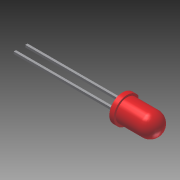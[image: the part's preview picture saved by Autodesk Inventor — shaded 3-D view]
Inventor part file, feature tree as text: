
AUTODESK INVENTOR PART (.ipt)
format: ipt  version: 2015 (Build 190159000, 159)  size: 212,992 bytes
history: native  units: mm
features: other x99, extrude x2, revolve x1, sketch x1, projected_geometry x1
ambient origin geometry x8: Origin, YZ Plane, XZ Plane, XY Plane, X Axis, Y Axis, Z Axis, Center Point
bodies: Solid1 (feature_tree)
feature tree (104):
  other  "Table"
  other  "LED Heigth mm 1.0"
  other  "LED Heigth mm 1.2"
  other  "LED Heigth mm 1.4"
  other  "LED Heigth mm 1.6"
  other  "LED Heigth mm 1.8"
  other  "LED Heigth mm 2.0"
  other  "LED Heigth mm 2.2"
  other  "LED Heigth mm 2.4"
  other  "LED Heigth mm 2.6"
  other  "LED  Heigth mm 2.8"
  other  "LED Heigth mm 3.0"
  other  "LED Heigth mm 3.2"
  other  "LED Heigth mm 3.4"
  other  "LED Heigth mm 3.6"
  other  "LED Heigth mm 3.8"
  other  "LED Heigth mm 4.0"
  other  "LED Heigth mm 4.2"
  other  "LED Heigth mm 4.4"
  other  "LED Heigth mm 4.6"
  other  "LED Heigth mm 4.8"
  other  "LED Heigth mm 5.0"
  other  "LED Heigth mm 5.2"
  other  "LED Heigth mm 5.4"
  other  "LED Heigth mm 5.6"
  other  "LED Heigth mm 5.8"
  other  "LED Heigth mm 6.0"
  other  "LED Heigth mm 6.2"
  other  "LED Heigth mm 6.4"
  other  "LED Heigth mm 6.6"
  other  "LED Heigth mm 6.8"
  other  "LED Heigth mm 7.0"
  other  "LED Heigth mm 7.2"
  other  "LED Heigth mm 7.4"
  other  "LED Heigth mm 7.6"
  other  "LED Heigth mm 7.8"
  other  "LED Heigth mm 8.0"
  other  "LED Heigth mm 8.2"
  other  "LED Heigth mm 8.4"
  other  "LED Heigth mm 8.6"
  other  "LED Heigth mm 8.8"
  other  "LED Heigth mm 9.0"
  other  "LED Heigth mm 9.2"
  other  "LED Heigth mm 9.4"
  other  "LED Heigth mm 9.6"
  other  "LED Heigth mm 9.8"
  other  "LED Heigth mm 10.0"
  other  "LED Heigth mm 10.2"
  other  "LED Heigth mm 10.4"
  other  "LED Heigth mm 10.6"
  other  "LED Heigth mm 10.8"
  other  "LED Heigth mm 11.0"
  other  "LED Heigth mm 11.2"
  other  "LED Heigth mm 11.4"
  other  "LED Heigth mm 11.6"
  other  "LED Heigth mm 11.8"
  other  "LED Heigth mm 12.0"
  other  "LED Heigth mm 12.2"
  other  "LED Heigth mm 12.4"
  other  "LED Heigth mm 12.6"
  other  "LED Heigth mm 12.8"
  other  "LED Heigth mm 13.0"
  other  "LED Heigth mm 13.2"
  other  "LED Heigth mm 13.4"
  other  "LED Heigth mm 13.6"
  other  "LED Heigth mm 13.8"
  other  "LED Heigth mm 14.0"
  other  "LED Heigth mm 14.2"
  other  "LED Heigth mm 14.4"
  other  "LED Heigth mm 14.6"
  other  "LED Heigth mm 14.8"
  other  "LED Heigth mm 15.0"
  other  "LED Heigth mm 15.2"
  other  "LED Heigth mm 15.4"
  other  "LED Heigth mm 15.6"
  other  "LED Heigth mm 15.8"
  other  "LED Heigth mm 16.0"
  other  "LED Heigth mm 16.2"
  other  "LED Heigth mm 16.4"
  other  "LED Heigth mm 16.6"
  other  "LED Heigth mm 16.8"
  other  "LED Heigth mm 17.0"
  other  "LED Heigth mm 17.2"
  other  "LED Heigth mm 17.4"
  other  "LED Heigth mm 17.6"
  other  "LED Heigth mm 17.8"
  other  "LED Heigth mm 18.0"
  other  "LED Heigth mm 18.2"
  other  "LED Heigth mm 18.4"
  other  "LED Heigth mm 18.6"
  other  "LED Heigth mm 18.8"
  other  "LED Heigth mm 19.0"
  other  "LED Heigth mm 19.2"
  other  "LED Heigth mm 19.4"
  other  "LED Heigth mm 19.6"
  other  "LED Heigth mm 19.8"
  other  "LED Heigth mm 20.0"
  revolve  "Revolution1"  [1 undecoded]
  extrude  "Extrusion1"  Depth=10.0mm
  extrude  "Extrusion2"  Depth=10.0mm
  other  "Work Axis1"
  other  "Work Axis2"
  sketch  "Sketch1"  dims[d1=2.95mm d2=1.0mm d3=5.0mm d4=8.6mm d5=2.5mm d6=90.0deg d7=0.5mm d8=0.5mm d9=1.27mm d10=1.27mm d12=0.0mm d13=20.0mm d14=0.0mm d15=0.0mm d16=10.0mm d17=0.0mm]
  projected_geometry  "Projected Loop1"
note: 1 required parameter value undecoded (feature->parameter linkage not recoverable at this tier; creation-order binding heuristic only, values carry confidence <= 0.55)
